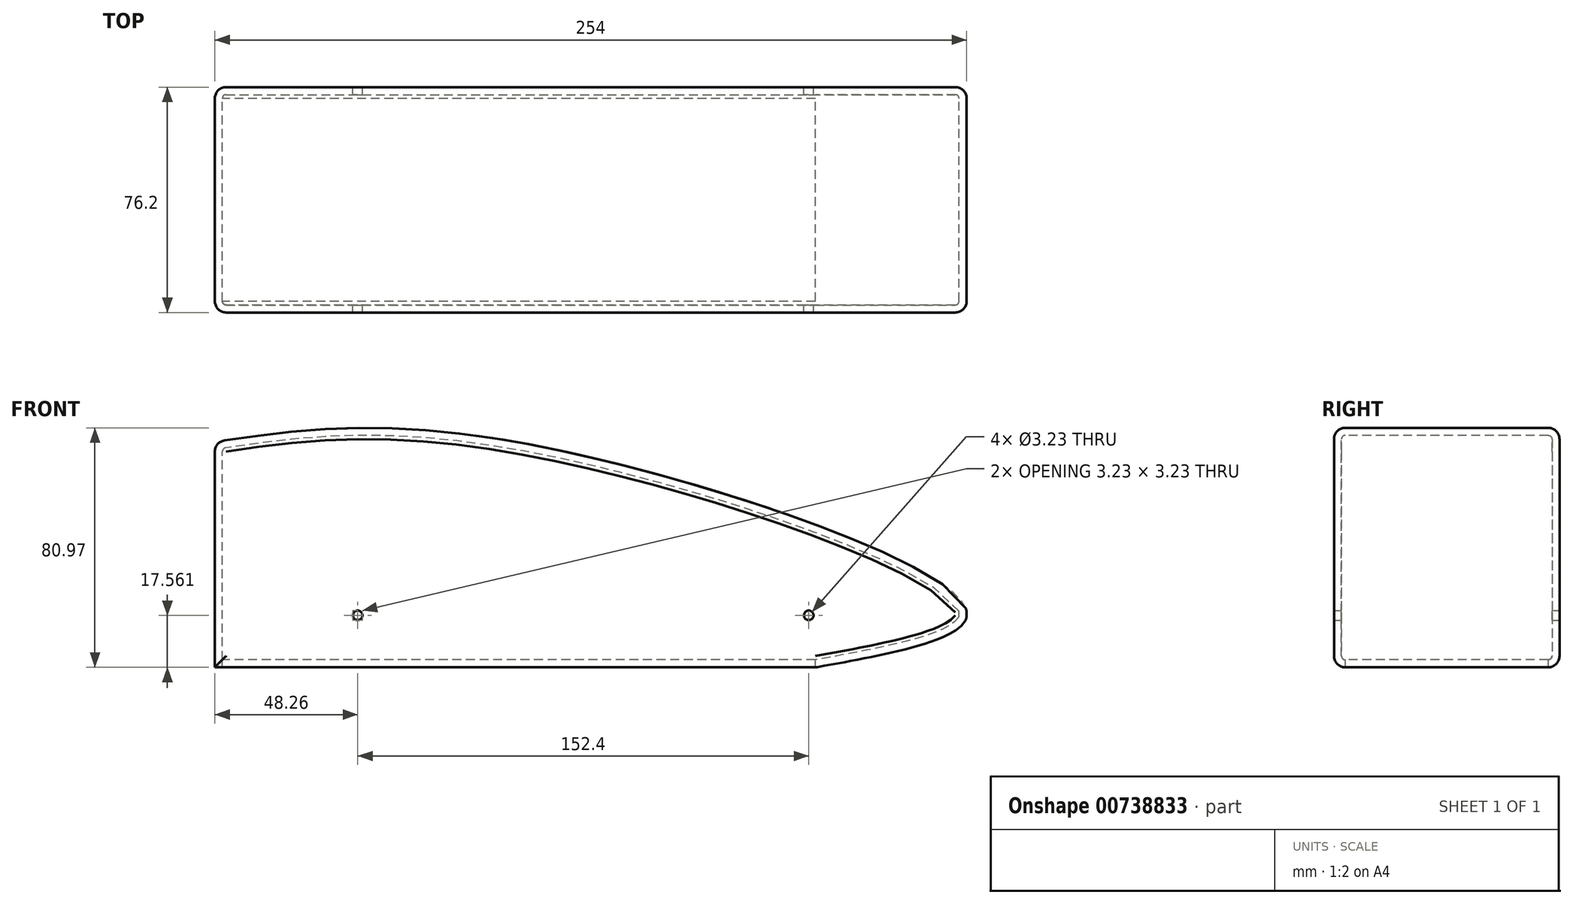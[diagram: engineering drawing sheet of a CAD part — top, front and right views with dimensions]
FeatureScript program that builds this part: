
annotation { "Feature Type Name" : "Feature", "Feature Type Description" : "" }
export const myFeature = defineFeature(function(context is Context, id is Id, definition is map)
    precondition{}
    {
        {
            var Q0;
            Q0=qCreatedBy(makeId("Top.planeOp"),FACE);
            var sketch = newSketch(context, id + "F0", { "sketchPlane" : qUnion([Q0])});
            skLineSegment(sketch, "E0.bottom", {"start": v(127, -38.1) * mm, "end": v(-127, -38.1) * mm});
            skLineSegment(sketch, "E0.top", {"start": v(127, 38.1) * mm, "end": v(-127, 38.1) * mm});
            skLineSegment(sketch, "E0.left", {"start": v(127, -38.1) * mm, "end": v(127, 38.1) * mm});
            skLineSegment(sketch, "E0.right", {"start": v(-127, -38.1) * mm, "end": v(-127, 38.1) * mm});
            skPoint(sketch, "E0.middle", {"position": v(0, 0) * mm});
            skSolve(sketch);
        }
        {
            var Q0;
            Q0=makeQuery(id+"F0.imprint","IMPRINT",FACE,{"disambiguationData":[TD([[makeQuery(id+"F0.imprint","IMPRINT",EDGE,{"derivedFrom":sQuery(id+"F0.wireOp",EDGE,"E0.bottom")}),-1.0]])]});
            extrude(context, id + "F1", {"entities" : qUnion([Q0]), "depth" : 101.6 * mm, "offsetDistance" : 25.4 * mm});
        }
        {
            var Q0;
            Q0=makeQuery(id+"F1.opExtrude","SWEPT_FACE",FACE,{"disambiguationData":[OSD([sQuery(id+"F0.wireOp",EDGE,"E0.bottom")])]});
            var sketch = newSketch(context, id + "F2", { "sketchPlane" : qUnion([Q0])});
            skFitSpline(sketch, "E1", {"points": [v(76.2, 0) * mm, v(127, 19.05) * mm, v(-25.4, 76.2) * mm, v(-127, 76.2) * mm], "startDerivative": vector(325.74, 59.04) * mm, "endDerivative": vector(-247.12, -37.15) * mm});
            skSolve(sketch);
        }
        {
            var Q0;
            {var subQ1=sQuery(id+"F0.wireOp",EDGE,"E0.bottom");var subQ6=makeQuery(id+"F1.opExtrude","CAP_EDGE",EDGE,{"disambiguationData":[OSD([subQ1])],"isStart":false});Q0=makeQuery(id+"F2.imprint","IMPRINT",FACE,{"disambiguationData":[TD([[makeQuery(id+"F2.imprint","IMPRINT",EDGE,{"derivedFrom":subQ6}),1.0]])]});}
            var Q1;
            {var subQ0=sQuery(id+"F2.wireOp",EDGE,"E1");var subQ1=sQuery(id+"F0.wireOp",EDGE,"E0.bottom");var subQ2=makeQuery(id+"F1.opExtrude","CAP_EDGE",EDGE,{"disambiguationData":[OSD([subQ1])],"isStart":true});var subQ3=makeQuery(id+"F2.imprint","INTERSECT",VERTEX,{"derivedFrom":[subQ2,subQ0]});Q1=makeQuery(id+"F2.imprint","IMPRINT",FACE,{"disambiguationData":[TD([[makeQuery(id+"F2.imprint","IMPRINT",EDGE,{"disambiguationData":[TD([[subQ3,-1.0]])],"derivedFrom":subQ0}),-1.0]])]});}
            extrude(context, id + "F3", {"entities" : qUnion([Q0, Q1]), "operationType" : NewBodyOperationType.REMOVE, "oppositeDirection" : true, "depth" : 76.2 * mm, "offsetDistance" : 25.4 * mm});
        }
        {
            var Q0;
            {var subQ0=sQuery(id+"F2.wireOp",EDGE,"E1");var subQ1=sQuery(id+"F0.wireOp",EDGE,"E0.bottom");Q0=makeQuery(id+"F3.boolean.opBoolean","COPY",FACE,{"derivedFrom":makeQuery(id+"F3.opExtrude","SWEPT_FACE",FACE,{"disambiguationData":[OSD([subQ0]),TDD([makeQuery(id+"F2.imprint","IMPRINT",EDGE,{"disambiguationData":[TD([[makeQuery(id+"F2.imprint","INTERSECT",VERTEX,{"derivedFrom":[makeQuery(id+"F1.opExtrude","SWEPT_EDGE",EDGE,{"disambiguationData":[OSD([subQ1,sQuery(id+"F0.wireOp",EDGE,"E0.right")])]}),subQ0]}),1.0]])],"derivedFrom":subQ0})])]})});}
            var Q1;
            {var subQ0=sQuery(id+"F2.wireOp",EDGE,"E1");var subQ1=sQuery(id+"F0.wireOp",EDGE,"E0.bottom");Q1=makeQuery(id+"F3.boolean.opBoolean","COPY",FACE,{"derivedFrom":makeQuery(id+"F3.opExtrude","SWEPT_FACE",FACE,{"disambiguationData":[OSD([subQ0]),TDD([makeQuery(id+"F2.imprint","IMPRINT",EDGE,{"disambiguationData":[TD([[makeQuery(id+"F2.imprint","INTERSECT",VERTEX,{"derivedFrom":[makeQuery(id+"F1.opExtrude","CAP_EDGE",EDGE,{"disambiguationData":[OSD([subQ1])],"isStart":true}),subQ0]}),-1.0]])],"derivedFrom":subQ0})])]})});}
            var Q2;
            {var subQ0=sQuery(id+"F2.wireOp",EDGE,"E1");var subQ1=sQuery(id+"F0.wireOp",EDGE,"E0.left");var subQ2=sQuery(id+"F0.wireOp",EDGE,"E0.bottom");Q2=makeQuery(id+"F3.boolean.opBoolean","COPY",EDGE,{"derivedFrom":makeQuery(id+"F3.opExtrude","SWEPT_EDGE",EDGE,{"disambiguationData":[OSD([subQ2,subQ1,subQ0]),TDD([makeQuery(id+"F2.imprint","INTERSECT",VERTEX,{"disambiguationData":[OD(1.0)],"derivedFrom":[makeQuery(id+"F1.opExtrude","SWEPT_EDGE",EDGE,{"disambiguationData":[OSD([subQ2,subQ1])]}),subQ0]})])]})});}
            var Q3;
            Q3=makeQuery(id+"F1.opExtrude","SWEPT_FACE",FACE,{"disambiguationData":[OSD([sQuery(id+"F0.wireOp",EDGE,"E0.top")])]});
            var Q4;
            Q4=makeQuery(id+"F1.opExtrude","SWEPT_FACE",FACE,{"disambiguationData":[OSD([sQuery(id+"F0.wireOp",EDGE,"E0.bottom")])]});
            fillet(context, id + "F4", {"entities" : qUnion([Q0, Q1, Q2, Q3, Q4]), "radius" : 3.8 * mm, "tangentPropagation" : true, "allowEdgeOverflow" : false});
        }
        {
            var Q0;
            Q0=makeQuery(id+"F1.opExtrude","CAP_FACE",FACE,{"disambiguationData":[OSD([sQuery(id+"F0.wireOp",EDGE,"E0.bottom"),sQuery(id+"F0.wireOp",EDGE,"E0.top"),sQuery(id+"F0.wireOp",EDGE,"E0.left"),sQuery(id+"F0.wireOp",EDGE,"E0.right")])],"isStart":true});
            shell(context, id + "F5", {"entities" : qUnion([Q0]), "thickness" : 2.54 * mm});
        }
        {
            var Q0;
            Q0=makeQuery(id+"F1.opExtrude","SWEPT_FACE",FACE,{"disambiguationData":[OSD([sQuery(id+"F0.wireOp",EDGE,"E0.top")])]});
            var sketch = newSketch(context, id + "F6", { "sketchPlane" : qUnion([Q0])});
            skPoint(sketch, "E2", {"position": v(-73.66, 17.56) * mm});
            skPoint(sketch, "E3", {"position": v(78.74, 17.56) * mm});
            skSolve(sketch);
        }
        {
            var Q0;
            Q0=sQuery(id+"F6.wireOp",VERTEX,"E2");
            var Q1;
            Q1=sQuery(id+"F6.wireOp",VERTEX,"E3");
            var Q2;
            Q2=makeQuery(id+"F1.opExtrude","SWEPT_BODY",BODY,{"disambiguationData":[OSD([sQuery(id+"F0.wireOp",EDGE,"E0.bottom"),sQuery(id+"F0.wireOp",EDGE,"E0.top"),sQuery(id+"F0.wireOp",EDGE,"E0.left"),sQuery(id+"F0.wireOp",EDGE,"E0.right")])]});
            hole(context, id + "F7", {"style" : HoleStyle.SIMPLE, "endStyle" : HoleEndStyle.BLIND, "holeDiameter" : 3.23 * mm, "majorDiameter" : 6.35 * mm, "holeDepth" : 76.2 * mm, "isTappedThrough" : true, "tappedDepth" : 12.7 * mm, "tapClearance" : 3, "startFromSketch" : true, "locations" : qUnion([Q0, Q1]), "scope" : qUnion([Q2])});
        }
    });
